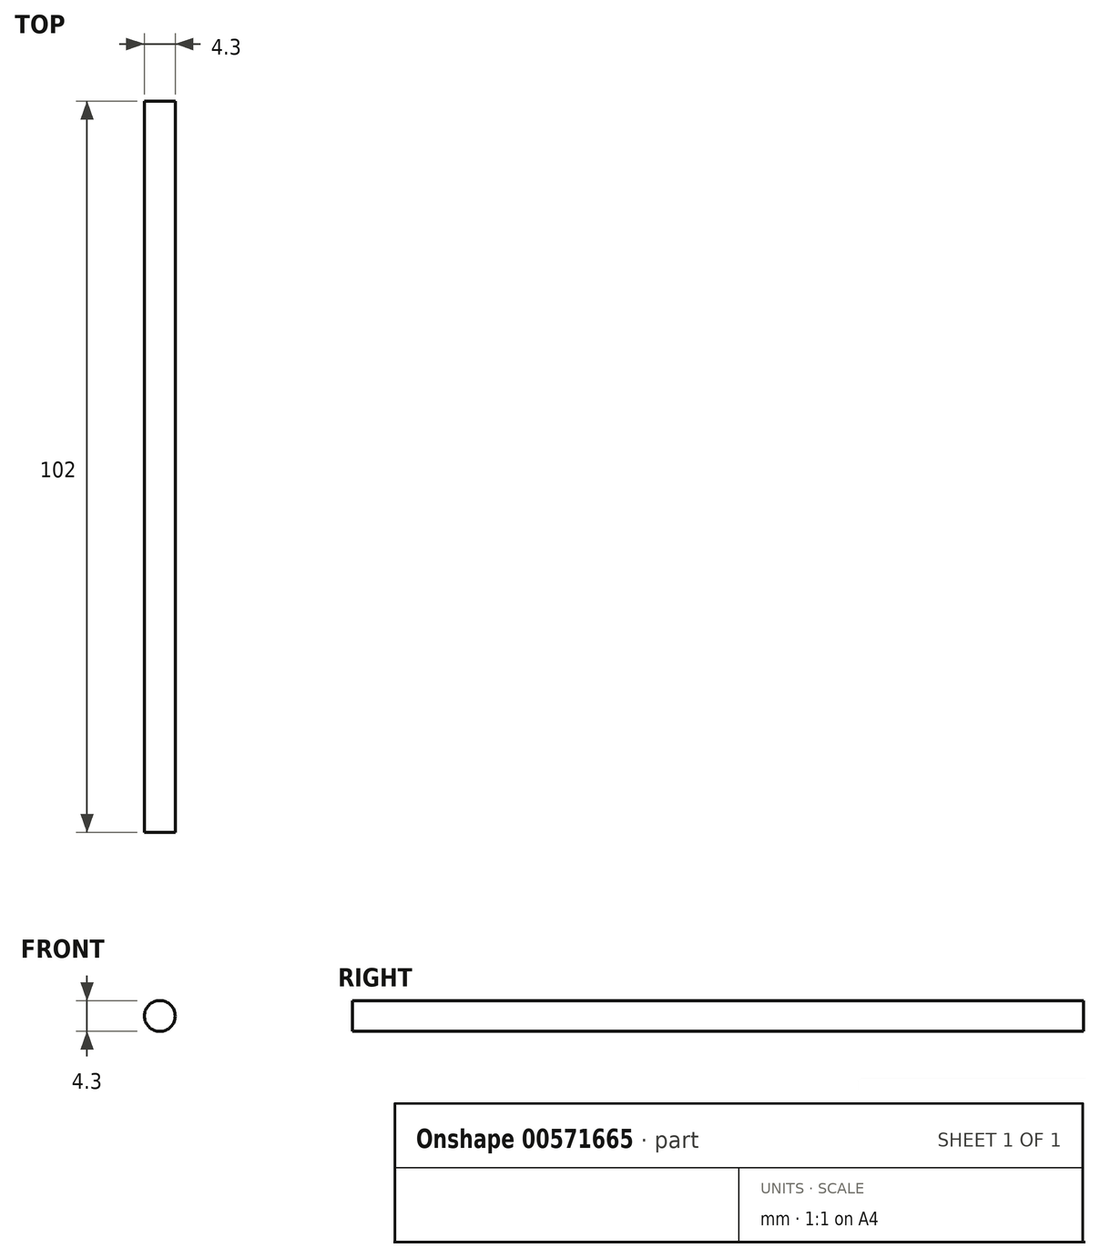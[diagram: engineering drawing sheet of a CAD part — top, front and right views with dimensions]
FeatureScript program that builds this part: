
annotation { "Feature Type Name" : "Feature", "Feature Type Description" : "" }
export const myFeature = defineFeature(function(context is Context, id is Id, definition is map)
    precondition{}
    {
        {
            var Q0;
            Q0=qCreatedBy(makeId("Front.planeOp"),FACE);
            var sketch = newSketch(context, id + "F0", { "sketchPlane" : qUnion([Q0])});
            skCircle(sketch, "E0", {"center": v(0, 0) * mm, "radius": 2.15 * mm});
            skSolve(sketch);
        }
        {
            var Q0;
            Q0 = qSketchRegion(id + "F0", true);
            extrude(context, id + "F1", {"entities" : qUnion([Q0]), "depth" : 102 * mm, "offsetDistance" : 25.4 * mm});
        }
    });
